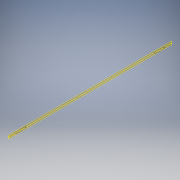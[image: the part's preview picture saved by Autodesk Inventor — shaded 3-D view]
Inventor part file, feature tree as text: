
AUTODESK INVENTOR PART (.ipt)
format: ipt  version: 2016 (Build 200138000, 138)  size: 207,360 bytes
history: native  units: mm
features: sketch x3, sweep x1, extrude x1, mirror x1
ambient origin geometry x8: Origin, YZ Plane, XZ Plane, XY Plane, X Axis, Y Axis, Z Axis, Center Point
bodies: Solid1 (feature_tree)
feature tree (6):
  sketch  "Sketch1"  dims[d0=6.0mm d1=150.0mm]
  sweep  "Sweep1"
  extrude  "Extrusion1"  TaperAngle=0.0deg  [1 undecoded]
  mirror  "Mirror1"
  sketch  "Sketch2"  dims[d2=6.0mm d3=0.0mm d4=0.0mm]
  sketch  "Sketch3"  dims[d5=1000.0mm d6=0.0mm]
note: 1 required parameter value undecoded (feature->parameter linkage not recoverable at this tier; creation-order binding heuristic only, values carry confidence <= 0.55)
